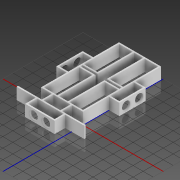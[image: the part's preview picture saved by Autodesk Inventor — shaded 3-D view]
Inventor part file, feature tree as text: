
AUTODESK INVENTOR PART (.ipt)
format: ipt  version: 2020.2 (Build 242310000, 310)  size: 325,632 bytes
history: native  units: mm
features: extrude x11, sketch x10
ambient origin geometry x8: Origin, YZ Plane, XZ Plane, XY Plane, X Axis, Y Axis, Z Axis, Center Point
bodies: Solid1 (feature_tree)
feature tree (21):
  sketch  "Sketch1"  dims[d1=156.0mm d12=3.0mm]
  extrude  "Extrusion1"  Depth=3.0mm
  sketch  "Sketch5"  dims[d13=3.0mm d15=70.0mm]
  extrude  "Extrusion6"  Depth=70.0mm
  sketch  "Sketch6"  dims[d17=70.0mm d18=23.0mm d19=0.0mm]
  extrude  "Extrusion7"  Depth=23.0mm TaperAngle=0.0deg
  extrude  "Extrusion10"  Depth=3.0mm
  extrude  "Extrusion9"  Depth=21.0mm TaperAngle=0.0deg
  extrude  "Extrusion11"  Depth=35.0mm
  extrude  "Extrusion12"  Depth=3.0mm
  extrude  "Extrusion13"  Depth=3.0mm
  extrude  "Extrusion14"  Depth=16.0mm
  extrude  "Extrusion15"  Depth=18.0mm
  extrude  "Extrusion16"  TaperAngle=180.0deg  [1 undecoded]
  sketch  "Sketch7"  dims[d66=3.0mm d68=3.0mm]
  sketch  "Sketch9"  dims[d80=21.0mm d81=0.0mm d92=24.25mm d93=0.0mm]
  sketch  "Sketch10"  dims[d97=35.0mm d98=35.0mm]
  sketch  "Sketch11"  dims[d99=3.0mm d100=3.0mm]
  sketch  "Sketch12"  dims[d101=3.0mm d102=3.0mm]
  sketch  "Sketch13"  dims[d108=16.0mm d109=16.0mm]
  sketch  "Sketch14"  dims[d110=10.0mm d111=0.0mm d112=18.0mm d113=180.0deg d114=3.0mm d115=21.0mm d116=23.5mm d117=0.0mm d118=13.4mm d119=11.5mm d120=13.4mm d121=11.5mm d122=16.0mm d123=13.4mm d124=11.5mm d125=16.0mm d126=10.0mm d127=0.0mm d128=25.0mm d129=3.0mm d130=25.0mm d131=3.0mm d132=23.0mm d133=0.0mm d134=3.0mm d135=47.5mm d136=87.5mm d137=0.0mm d138=0.0mm d139=38.1mm d140=3.0mm d141=38.1mm d142=3.0mm d143=21.0mm d144=0.0mm d145=3.0mm d146=60.25mm d147=0.0mm d148=17.0mm d149=11.5mm d150=16.0mm d151=17.0mm d152=11.5mm d153=16.0mm d154=10.0mm d155=0.0mm]
note: 1 required parameter value undecoded (feature->parameter linkage not recoverable at this tier; creation-order binding heuristic only, values carry confidence <= 0.55)
